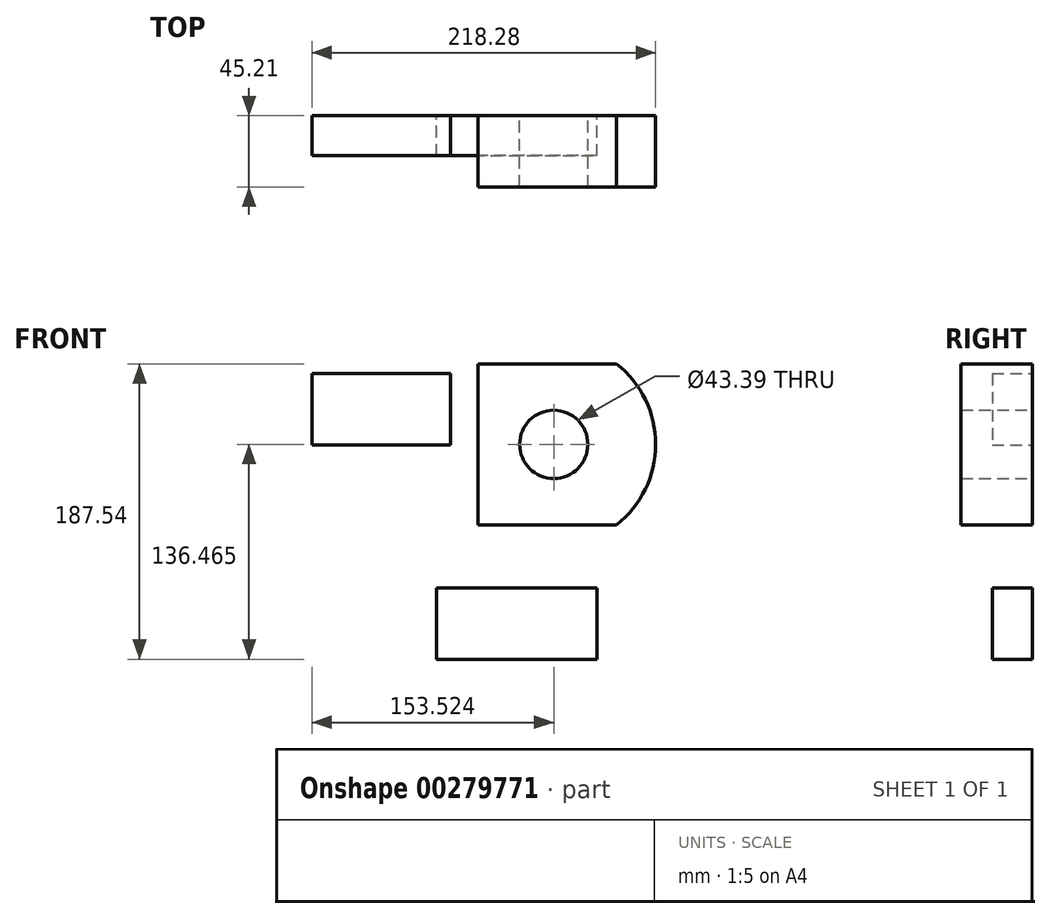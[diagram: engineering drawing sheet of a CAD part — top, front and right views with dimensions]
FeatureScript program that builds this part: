
annotation { "Feature Type Name" : "Feature", "Feature Type Description" : "" }
export const myFeature = defineFeature(function(context is Context, id is Id, definition is map)
    precondition{}
    {
        {
            var Q0;
            Q0=qCreatedBy(makeId("Front.planeOp"),FACE);
            var sketch = newSketch(context, id + "F0", { "sketchPlane" : qUnion([Q0])});
            skLineSegment(sketch, "E0", {"start": v(-153.09, -122.27) * mm, "end": v(-51.23, -122.27) * mm});
            skLineSegment(sketch, "E1", {"start": v(-51.23, -122.27) * mm, "end": v(-51.23, -77.06) * mm});
            skLineSegment(sketch, "E2", {"start": v(-51.23, -77.06) * mm, "end": v(-153.09, -77.06) * mm});
            skLineSegment(sketch, "E3", {"start": v(-153.09, -77.06) * mm, "end": v(-153.09, -122.27) * mm});
            skSolve(sketch);
        }
        {
            var Q0;
            Q0=qCreatedBy(makeId("Front.planeOp"),FACE);
            var sketch = newSketch(context, id + "F1", { "sketchPlane" : qUnion([Q0])});
            skLineSegment(sketch, "E4", {"start": v(-232.08, 59.1) * mm, "end": v(-232.08, 13.89) * mm});
            skLineSegment(sketch, "E5", {"start": v(-232.08, 59.1) * mm, "end": v(-144.25, 59.1) * mm});
            skLineSegment(sketch, "E6", {"start": v(-144.25, 59.1) * mm, "end": v(-144.25, 13.89) * mm});
            skLineSegment(sketch, "E7", {"start": v(-144.25, 13.89) * mm, "end": v(-232.08, 13.89) * mm});
            skSolve(sketch);
        }
        {
            var Q0;
            Q0=qCreatedBy(makeId("Front.planeOp"),FACE);
            var sketch = newSketch(context, id + "F2", { "sketchPlane" : qUnion([Q0])});
            skLineSegment(sketch, "E8", {"start": v(-126.58, -36.88) * mm, "end": v(-38.76, -36.88) * mm});
            skLineSegment(sketch, "E9", {"start": v(-126.58, -36.88) * mm, "end": v(-126.58, 65.27) * mm});
            skLineSegment(sketch, "E10", {"start": v(-126.58, 65.27) * mm, "end": v(-38.76, 65.27) * mm});
            skArc(sketch, "E11", {"start": v(-38.76, -36.88) * mm, "mid": v(-13.8, 14.2) * mm, "end": v(-38.76, 65.27) * mm});
            skCircle(sketch, "E12", {"center": v(-78.56, 14.2) * mm, "radius": 21.7 * mm});
            skCircle(sketch, "E13", {"center": v(-78.56, 14.2) * mm, "radius": 18.4 * mm});
            skSolve(sketch);
        }
        {
            var Q0;
            Q0 = qSketchRegion(id + "F2", true);
            extrude(context, id + "F3", {"entities" : qUnion([Q0]), "depth" : 45.2 * mm});
        }
        {
            var Q0;
            Q0=makeQuery(id+"F1.imprint","IMPRINT",FACE,{"disambiguationData":[TD([[makeQuery(id+"F1.imprint","IMPRINT",EDGE,{"derivedFrom":sQuery(id+"F1.wireOp",EDGE,"E4")}),1.0]])]});
            extrude(context, id + "F4", {"entities" : qUnion([Q0]), "depth" : 25.4 * mm});
        }
        {
            var Q0;
            Q0=makeQuery(id+"F0.imprint","IMPRINT",FACE,{"disambiguationData":[TD([[makeQuery(id+"F0.imprint","IMPRINT",EDGE,{"derivedFrom":sQuery(id+"F0.wireOp",EDGE,"E0")}),1.0]])]});
            extrude(context, id + "F5", {"entities" : qUnion([Q0]), "depth" : 25.4 * mm});
        }
    });
